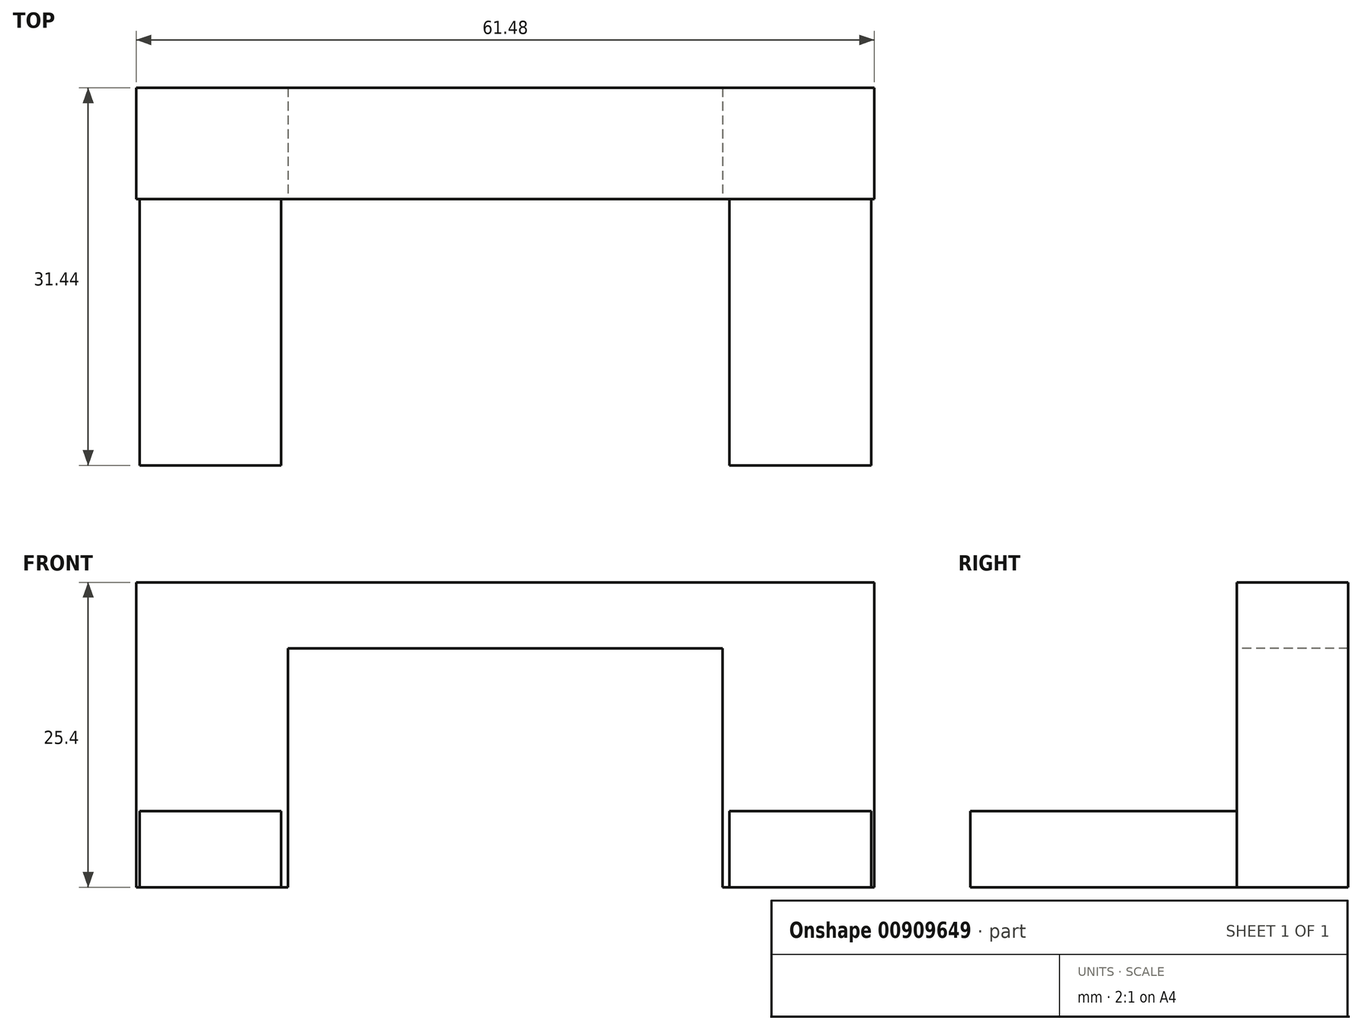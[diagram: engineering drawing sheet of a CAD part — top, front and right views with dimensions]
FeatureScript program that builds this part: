
annotation { "Feature Type Name" : "Feature", "Feature Type Description" : "" }
export const myFeature = defineFeature(function(context is Context, id is Id, definition is map)
    precondition{}
    {
        {
            var Q0;
            Q0=qCreatedBy(makeId("Top.planeOp"),FACE);
            var sketch = newSketch(context, id + "F0", { "sketchPlane" : qUnion([Q0])});
            skLineSegment(sketch, "E0.bottom", {"start": v(-30.74, 38.6) * mm, "end": v(30.74, 38.6) * mm});
            skLineSegment(sketch, "E0.top", {"start": v(-30.74, 29.34) * mm, "end": v(30.74, 29.34) * mm});
            skLineSegment(sketch, "E0.left", {"start": v(-30.74, 38.6) * mm, "end": v(-30.74, 29.34) * mm});
            skLineSegment(sketch, "E0.right", {"start": v(30.74, 38.6) * mm, "end": v(30.74, 29.34) * mm});
            skSolve(sketch);
        }
        {
            var Q0;
            Q0=makeQuery(id+"F0.imprint","IMPRINT",FACE,{"disambiguationData":[TD([[makeQuery(id+"F0.imprint","IMPRINT",EDGE,{"derivedFrom":sQuery(id+"F0.wireOp",EDGE,"E0.bottom")}),-1.0]])]});
            extrude(context, id + "F1", {"entities" : qUnion([Q0]), "depth" : 25.4 * mm, "offsetDistance" : 25.4 * mm});
        }
        {
            var Q0;
            Q0=qCreatedBy(makeId("Top.planeOp"),FACE);
            var sketch = newSketch(context, id + "F2", { "sketchPlane" : qUnion([Q0])});
            skLineSegment(sketch, "E1.bottom", {"start": v(-30.46, 29.9) * mm, "end": v(-18.67, 29.9) * mm});
            skLineSegment(sketch, "E1.top", {"start": v(-30.46, 7.16) * mm, "end": v(-18.67, 7.16) * mm});
            skLineSegment(sketch, "E1.left", {"start": v(-30.46, 29.9) * mm, "end": v(-30.46, 7.16) * mm});
            skLineSegment(sketch, "E1.right", {"start": v(-18.67, 29.9) * mm, "end": v(-18.67, 7.16) * mm});
            skLineSegment(sketch, "E2.MirrorCS", {"start": v(18.67, 29.9) * mm, "end": v(18.67, 7.16) * mm});
            skLineSegment(sketch, "E3.MirrorCS", {"start": v(30.46, 29.9) * mm, "end": v(30.46, 7.16) * mm});
            skLineSegment(sketch, "E4.MirrorCS", {"start": v(30.46, 7.16) * mm, "end": v(18.67, 7.16) * mm});
            skLineSegment(sketch, "E5.MirrorCS", {"start": v(30.46, 29.9) * mm, "end": v(18.67, 29.9) * mm});
            skSolve(sketch);
        }
        {
            var Q0;
            Q0=makeQuery(id+"F2.imprint","IMPRINT",FACE,{"disambiguationData":[TD([[makeQuery(id+"F2.imprint","IMPRINT",EDGE,{"derivedFrom":sQuery(id+"F2.wireOp",EDGE,"E1.bottom")}),-1.0]])]});
            var Q1;
            Q1=makeQuery(id+"F2.imprint","IMPRINT",FACE,{"disambiguationData":[TD([[makeQuery(id+"F2.imprint","IMPRINT",EDGE,{"derivedFrom":sQuery(id+"F2.wireOp",EDGE,"E2.MirrorCS")}),1.0]])]});
            extrude(context, id + "F3", {"entities" : qUnion([Q0, Q1]), "operationType" : NewBodyOperationType.ADD, "depth" : 6.35 * mm, "offsetDistance" : 25.4 * mm});
        }
        {
            var Q0;
            Q0=qCreatedBy(makeId("Front.planeOp"),FACE);
            var sketch = newSketch(context, id + "F4", { "sketchPlane" : qUnion([Q0])});
            skLineSegment(sketch, "E6.bottom", {"start": v(-18.1, 0) * mm, "end": v(18.1, 0) * mm});
            skLineSegment(sketch, "E6.top", {"start": v(-18.1, 19.9) * mm, "end": v(18.1, 19.9) * mm});
            skLineSegment(sketch, "E6.left", {"start": v(-18.1, 0) * mm, "end": v(-18.1, 19.9) * mm});
            skLineSegment(sketch, "E6.right", {"start": v(18.1, 0) * mm, "end": v(18.1, 19.9) * mm});
            skSolve(sketch);
        }
        {
            var Q0;
            Q0=makeQuery(id+"F4.imprint","IMPRINT",FACE,{"disambiguationData":[TD([[makeQuery(id+"F4.imprint","IMPRINT",EDGE,{"derivedFrom":sQuery(id+"F4.wireOp",EDGE,"E6.bottom")}),1.0]])]});
            extrude(context, id + "F5", {"entities" : qUnion([Q0]), "operationType" : NewBodyOperationType.REMOVE, "endBound" : BoundingType.THROUGH_ALL, "oppositeDirection" : true, "depth" : 25.4 * mm, "offsetDistance" : 25.4 * mm});
        }
    });
